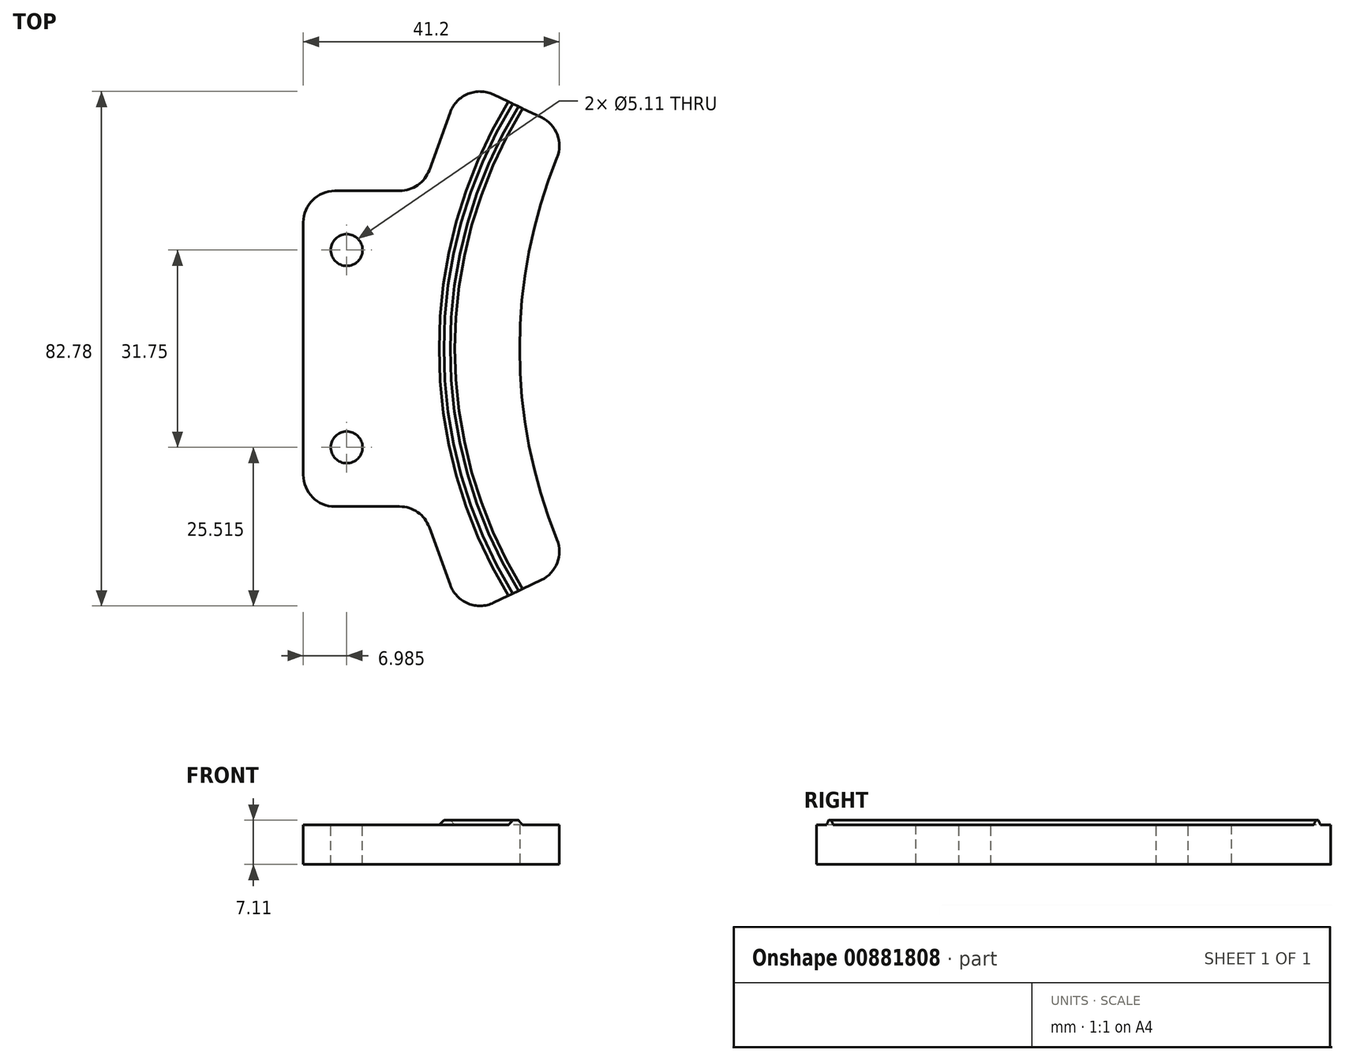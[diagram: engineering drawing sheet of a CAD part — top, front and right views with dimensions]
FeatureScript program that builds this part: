
annotation { "Feature Type Name" : "Feature", "Feature Type Description" : "" }
export const myFeature = defineFeature(function(context is Context, id is Id, definition is map)
    precondition{}
    {
        {
            var Q0;
            Q0=qCreatedBy(makeId("Top.planeOp"),FACE);
            var sketch = newSketch(context, id + "F0", { "sketchPlane" : qUnion([Q0])});
            skLineSegment(sketch, "E0", {"start": v(0, 25.4) * mm, "end": v(19.05, 25.4) * mm});
            skLineSegment(sketch, "E1", {"start": v(0, 25.4) * mm, "end": v(0, -25.4) * mm});
            skLineSegment(sketch, "E2", {"start": v(0, -25.4) * mm, "end": v(19.05, -25.4) * mm});
            skPoint(sketch, "E3", {"position": v(0, 0) * mm});
            skArc(sketch, "E4", {"start": v(42.76, 35.1) * mm, "mid": v(34.81, 0) * mm, "end": v(42.76, -35.1) * mm});
            skLineSegment(sketch, "E5", {"start": v(42.76, -35.1) * mm, "end": v(25.57, -43.3) * mm});
            skLineSegment(sketch, "E6", {"start": v(25.57, -43.3) * mm, "end": v(19.05, -25.4) * mm});
            skLineSegment(sketch, "E7", {"start": v(42.76, 35.1) * mm, "end": v(25.57, 43.3) * mm});
            skLineSegment(sketch, "E8", {"start": v(25.57, 43.3) * mm, "end": v(19.05, 25.4) * mm});
            skLineSegment(sketch, "E9", {"start": v(0, 0) * mm, "end": v(116.3, 0) * mm, "construction": true});
            skLineSegment(sketch, "E10", {"start": v(42.76, 35.1) * mm, "end": v(45.5, 40.83) * mm, "construction": true});
            skSolve(sketch);
        }
        {
            var Q0;
            Q0=makeQuery(id+"F0.imprint","IMPRINT",FACE,{"disambiguationData":[TD([[makeQuery(id+"F0.imprint","IMPRINT",EDGE,{"derivedFrom":sQuery(id+"F0.wireOp",EDGE,"E0")}),-1.0]])]});
            extrude(context, id + "F1", {"entities" : qUnion([Q0]), "depth" : 6.35 * mm, "offsetDistance" : 25.4 * mm});
        }
        {
            var Q0;
            Q0=makeQuery(id+"F1.opExtrude","CAP_FACE",FACE,{"disambiguationData":[OSD([sQuery(id+"F0.wireOp",EDGE,"E0"),sQuery(id+"F0.wireOp",EDGE,"E1"),sQuery(id+"F0.wireOp",EDGE,"E2"),sQuery(id+"F0.wireOp",EDGE,"E4"),sQuery(id+"F0.wireOp",EDGE,"E5"),sQuery(id+"F0.wireOp",EDGE,"E6"),sQuery(id+"F0.wireOp",EDGE,"E7"),sQuery(id+"F0.wireOp",EDGE,"E8")])],"isStart":false});
            var sketch = newSketch(context, id + "F2", { "sketchPlane" : qUnion([Q0])});
            skArc(sketch, "E11", {"start": v(34.16, 39.2) * mm, "mid": v(23.13, 0) * mm, "end": v(34.16, -39.2) * mm, "construction": true});
            skArc(sketch, "E12.0", {"start": v(33, 39.75) * mm, "mid": v(21.86, 0) * mm, "end": v(33, -39.75) * mm});
            skArc(sketch, "E13.0", {"start": v(35.31, 38.65) * mm, "mid": v(24.4, 0) * mm, "end": v(35.31, -38.65) * mm});
            skLineSegment(sketch, "E14", {"start": v(33, 39.75) * mm, "end": v(35.31, 38.65) * mm});
            skLineSegment(sketch, "E15", {"start": v(33, -39.75) * mm, "end": v(35.31, -38.65) * mm});
            skSolve(sketch);
        }
        {
            var Q0;
            Q0=makeQuery(id+"F2.imprint","IMPRINT",FACE,{"disambiguationData":[TD([[makeQuery(id+"F2.imprint","IMPRINT",EDGE,{"derivedFrom":sQuery(id+"F2.wireOp",EDGE,"E12.0")}),1.0]])]});
            extrude(context, id + "F3", {"entities" : qUnion([Q0]), "operationType" : NewBodyOperationType.ADD, "depth" : 0.76 * mm, "offsetDistance" : 25.4 * mm});
        }
        {
            var Q0;
            Q0=makeQuery(id+"F3.opExtrude","CAP_EDGE",EDGE,{"disambiguationData":[OSD([sQuery(id+"F2.wireOp",EDGE,"E12.0")])],"isStart":false});
            var Q1;
            Q1=makeQuery(id+"F3.opExtrude","CAP_EDGE",EDGE,{"disambiguationData":[OSD([sQuery(id+"F2.wireOp",EDGE,"E13.0")])],"isStart":false});
            chamfer(context, id + "F4", {"entities" : qUnion([Q0, Q1]), "width" : 0.76 * mm, "tangentPropagation" : true});
        }
        {
            var Q0;
            {var subQ0=sQuery(id+"F0.wireOp",EDGE,"E5");var subQ1=sQuery(id+"F0.wireOp",EDGE,"E2");var subQ2=sQuery(id+"F0.wireOp",EDGE,"E1");var subQ3=sQuery(id+"F0.wireOp",EDGE,"E0");var subQ4=sQuery(id+"F0.wireOp",EDGE,"E6");var subQ5=sQuery(id+"F0.wireOp",EDGE,"E7");var subQ6=sQuery(id+"F0.wireOp",EDGE,"E8");Q0=makeQuery(id+"F3.boolean.opBoolean","SPLIT",FACE,{"disambiguationData":[TD([makeQuery(id+"F1.opExtrude","SWEPT_FACE",FACE,{"disambiguationData":[OSD([subQ3])]})])],"derivedFrom":makeQuery(id+"F1.opExtrude","CAP_FACE",FACE,{"disambiguationData":[OSD([subQ3,subQ2,subQ1,sQuery(id+"F0.wireOp",EDGE,"E4"),subQ0,subQ4,subQ5,subQ6])],"isStart":false})});}
            var sketch = newSketch(context, id + "F5", { "sketchPlane" : qUnion([Q0])});
            skCircle(sketch, "E16", {"center": v(6.99, 15.88) * mm, "radius": 2.55 * mm});
            skCircle(sketch, "E17", {"center": v(6.99, -15.88) * mm, "radius": 2.55 * mm});
            skLineSegment(sketch, "E18", {"start": v(0, 0) * mm, "end": v(34.81, 0) * mm, "construction": true});
            skSolve(sketch);
        }
        {
            var Q0;
            Q0=makeQuery(id+"F5.imprint","IMPRINT",FACE,{"disambiguationData":[TD([[makeQuery(id+"F5.imprint","IMPRINT",EDGE,{"derivedFrom":sQuery(id+"F5.wireOp",EDGE,"E16")}),1.0]])]});
            var Q1;
            Q1=makeQuery(id+"F5.imprint","IMPRINT",FACE,{"disambiguationData":[TD([[makeQuery(id+"F5.imprint","IMPRINT",EDGE,{"derivedFrom":sQuery(id+"F5.wireOp",EDGE,"E17")}),1.0]])]});
            extrude(context, id + "F6", {"entities" : qUnion([Q0, Q1]), "operationType" : NewBodyOperationType.REMOVE, "endBound" : BoundingType.THROUGH_ALL, "oppositeDirection" : true, "depth" : 25.4 * mm, "offsetDistance" : 25.4 * mm});
        }
        {
            var Q0;
            Q0=makeQuery(id+"F1.opExtrude","SWEPT_EDGE",EDGE,{"disambiguationData":[OSD([sQuery(id+"F0.wireOp",EDGE,"E1"),sQuery(id+"F0.wireOp",EDGE,"E2")])]});
            var Q1;
            Q1=makeQuery(id+"F1.opExtrude","SWEPT_EDGE",EDGE,{"disambiguationData":[OSD([sQuery(id+"F0.wireOp",EDGE,"E2"),sQuery(id+"F0.wireOp",EDGE,"E6")])]});
            var Q2;
            Q2=makeQuery(id+"F1.opExtrude","SWEPT_EDGE",EDGE,{"disambiguationData":[OSD([sQuery(id+"F0.wireOp",EDGE,"E5"),sQuery(id+"F0.wireOp",EDGE,"E6")])]});
            var Q3;
            Q3=makeQuery(id+"F1.opExtrude","SWEPT_EDGE",EDGE,{"disambiguationData":[OSD([sQuery(id+"F0.wireOp",EDGE,"E4"),sQuery(id+"F0.wireOp",EDGE,"E5")])]});
            var Q4;
            Q4=makeQuery(id+"F1.opExtrude","SWEPT_EDGE",EDGE,{"disambiguationData":[OSD([sQuery(id+"F0.wireOp",EDGE,"E0"),sQuery(id+"F0.wireOp",EDGE,"E1")])]});
            var Q5;
            Q5=makeQuery(id+"F1.opExtrude","SWEPT_EDGE",EDGE,{"disambiguationData":[OSD([sQuery(id+"F0.wireOp",EDGE,"E0"),sQuery(id+"F0.wireOp",EDGE,"E8")])]});
            var Q6;
            Q6=makeQuery(id+"F1.opExtrude","SWEPT_EDGE",EDGE,{"disambiguationData":[OSD([sQuery(id+"F0.wireOp",EDGE,"E7"),sQuery(id+"F0.wireOp",EDGE,"E8")])]});
            var Q7;
            Q7=makeQuery(id+"F1.opExtrude","SWEPT_EDGE",EDGE,{"disambiguationData":[OSD([sQuery(id+"F0.wireOp",EDGE,"E4"),sQuery(id+"F0.wireOp",EDGE,"E7")])]});
            fillet(context, id + "F7", {"entities" : qUnion([Q0, Q1, Q2, Q3, Q4, Q5, Q6, Q7]), "radius" : 5.08 * mm, "tangentPropagation" : true, "allowEdgeOverflow" : false});
        }
    });
